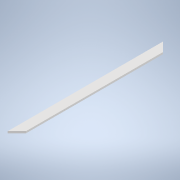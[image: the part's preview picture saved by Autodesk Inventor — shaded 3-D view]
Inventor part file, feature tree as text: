
AUTODESK INVENTOR PART (.ipt)
format: ipt  version: 2020 (Build 240168000, 168)  size: 102,912 bytes
history: native  units: mm
features: extrude x2, sketch x1
ambient origin geometry x8: Origin, YZ Plane, XZ Plane, XY Plane, X Axis, Y Axis, Z Axis, Center Point
bodies: Solid1 (feature_tree)
feature tree (3):
  sketch  "Sketch1"  dims[d0=1.0mm d1=0.0mm d2=45.0deg d3=45.0deg d4=45.0deg d5=1.0mm d6=0.0mm d7=5.0mm d9=75.0mm]
  extrude  "Extrusion1"  TaperAngle=45.0deg  [1 undecoded]
  extrude  "Extrusion2"  TaperAngle=45.0deg  [1 undecoded]
note: 2 required parameter values undecoded (feature->parameter linkage not recoverable at this tier; creation-order binding heuristic only, values carry confidence <= 0.55)
